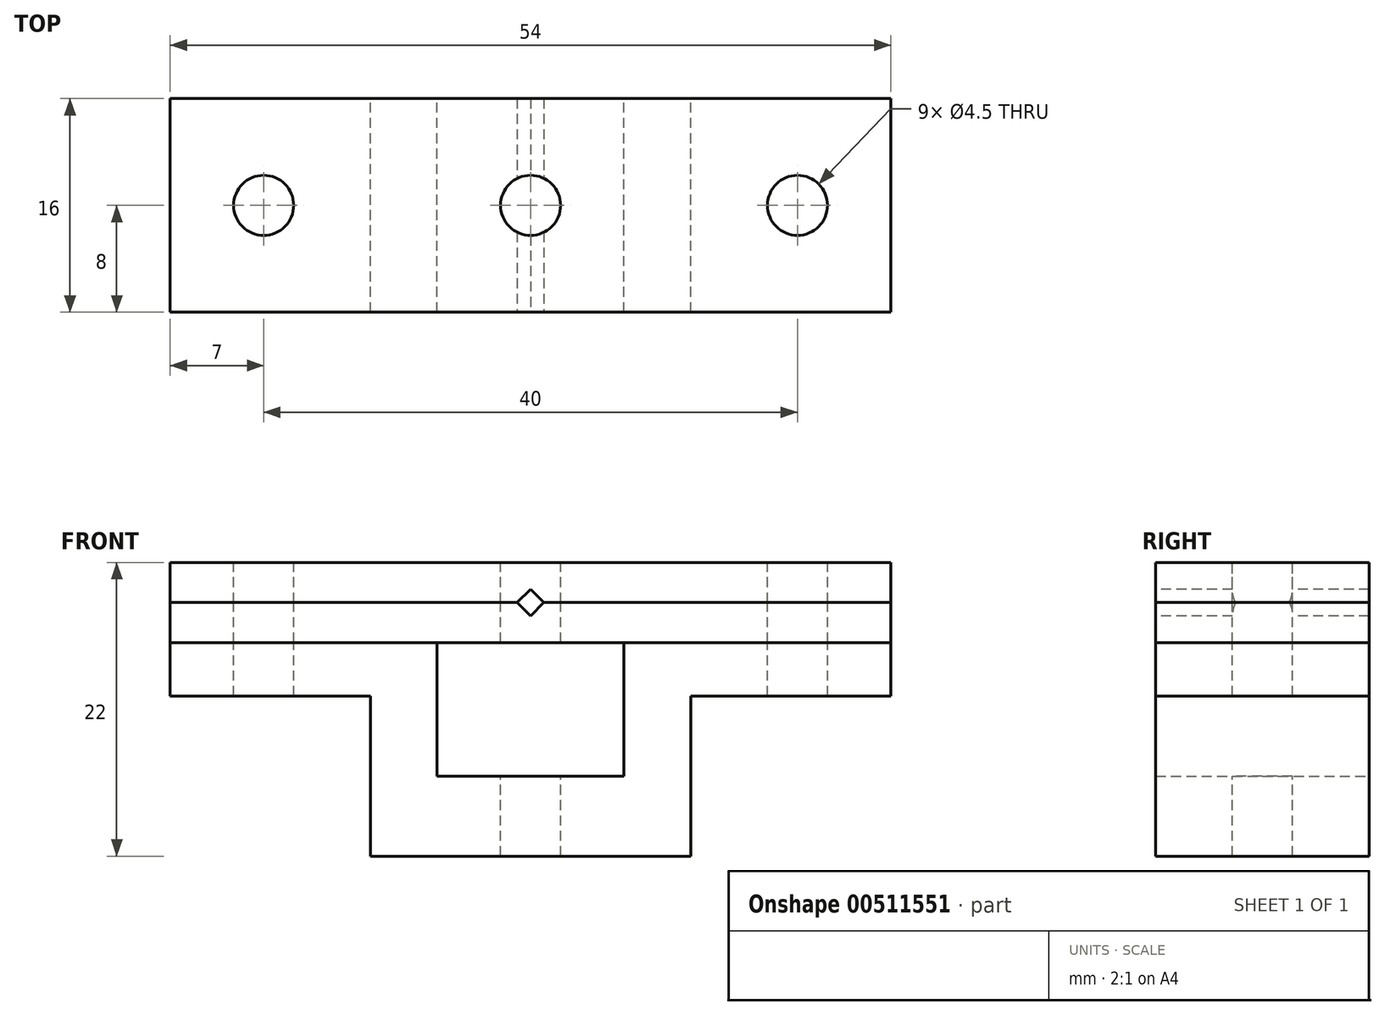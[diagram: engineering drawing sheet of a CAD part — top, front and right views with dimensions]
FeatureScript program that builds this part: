
annotation { "Feature Type Name" : "Feature", "Feature Type Description" : "" }
export const myFeature = defineFeature(function(context is Context, id is Id, definition is map)
    precondition{}
    {
        {
            var Q0;
            Q0=qCreatedBy(makeId("Front.planeOp"),FACE);
            var sketch = newSketch(context, id + "F0", { "sketchPlane" : qUnion([Q0])});
            skLineSegment(sketch, "E0", {"start": v(-7, 0) * mm, "end": v(-7, -10) * mm});
            skLineSegment(sketch, "E1", {"start": v(-7, -10) * mm, "end": v(7, -10) * mm});
            skLineSegment(sketch, "E2", {"start": v(7, -10) * mm, "end": v(7, 0) * mm});
            skLineSegment(sketch, "E3", {"start": v(7, 0) * mm, "end": v(27, 0) * mm});
            skLineSegment(sketch, "E4", {"start": v(27, 0) * mm, "end": v(27, -16) * mm});
            skLineSegment(sketch, "E5", {"start": v(27, -16) * mm, "end": v(-27, -16) * mm});
            skLineSegment(sketch, "E6", {"start": v(-27, -16) * mm, "end": v(-27, 0) * mm});
            skLineSegment(sketch, "E7", {"start": v(-27, 0) * mm, "end": v(-7, 0) * mm});
            skLineSegment(sketch, "E8.bottom", {"start": v(-27, 0) * mm, "end": v(27, 0) * mm});
            skLineSegment(sketch, "E8.top", {"start": v(-27, 3) * mm, "end": v(27, 3) * mm});
            skLineSegment(sketch, "E8.left", {"start": v(-27, 0) * mm, "end": v(-27, 3) * mm});
            skLineSegment(sketch, "E8.right", {"start": v(27, 0) * mm, "end": v(27, 3) * mm});
            skPoint(sketch, "E9.oppositeSnap0", {"position": v(27, 1.5) * mm});
            skLineSegment(sketch, "E9.top", {"start": v(-27, 6) * mm, "end": v(27, 6) * mm});
            skLineSegment(sketch, "E9.left", {"start": v(-27, 3) * mm, "end": v(-27, 6) * mm});
            skLineSegment(sketch, "E9.right", {"start": v(27, 3) * mm, "end": v(27, 6) * mm});
            skSolve(sketch);
        }
        {
            var Q0;
            Q0=makeQuery(id+"F0.imprint","IMPRINT",FACE,{"disambiguationData":[TD([[makeQuery(id+"F0.imprint","IMPRINT",EDGE,{"derivedFrom":sQuery(id+"F0.wireOp",EDGE,"E0")}),-1.0]])]});
            extrude(context, id + "F1", {"entities" : qUnion([Q0]), "endBound" : BoundingType.SYMMETRIC, "depth" : 16 * mm, "offsetDistance" : 25 * mm});
        }
        {
            var Q0;
            Q0=makeQuery(id+"F0.imprint","IMPRINT",FACE,{"disambiguationData":[TD([[makeQuery(id+"F0.imprint","IMPRINT",EDGE,{"derivedFrom":sQuery(id+"F0.wireOp",EDGE,"E3")}),1.0]])]});
            extrude(context, id + "F2", {"entities" : qUnion([Q0]), "endBound" : BoundingType.SYMMETRIC, "depth" : 16 * mm, "offsetDistance" : 25 * mm});
        }
        {
            var Q0;
            Q0=makeQuery(id+"F0.imprint","IMPRINT",FACE,{"disambiguationData":[TD([[makeQuery(id+"F0.imprint","IMPRINT",EDGE,{"derivedFrom":sQuery(id+"F0.wireOp",EDGE,"E8.top")}),1.0]])]});
            extrude(context, id + "F3", {"entities" : qUnion([Q0]), "endBound" : BoundingType.SYMMETRIC, "depth" : 16 * mm, "offsetDistance" : 25 * mm});
        }
        {
            var Q0;
            Q0=makeQuery(id+"F3.opExtrude","SWEPT_FACE",FACE,{"disambiguationData":[OSD([sQuery(id+"F0.wireOp",EDGE,"E9.top")])]});
            var sketch = newSketch(context, id + "F4", { "sketchPlane" : qUnion([Q0])});
            skCircle(sketch, "E10", {"center": v(0, 0) * mm, "radius": 2.25 * mm});
            skCircle(sketch, "E11", {"center": v(-20, 0) * mm, "radius": 2.25 * mm});
            skCircle(sketch, "E12", {"center": v(20, 0) * mm, "radius": 2.25 * mm});
            skSolve(sketch);
        }
        {
            var Q0;
            Q0=makeQuery(id+"F4.imprint","IMPRINT",FACE,{"disambiguationData":[TD([[makeQuery(id+"F4.imprint","IMPRINT",EDGE,{"derivedFrom":sQuery(id+"F4.wireOp",EDGE,"E11")}),1.0]])]});
            var Q1;
            Q1=makeQuery(id+"F4.imprint","IMPRINT",FACE,{"disambiguationData":[TD([[makeQuery(id+"F4.imprint","IMPRINT",EDGE,{"derivedFrom":sQuery(id+"F4.wireOp",EDGE,"E12")}),1.0]])]});
            var Q2;
            Q2=makeQuery(id+"F4.imprint","IMPRINT",FACE,{"disambiguationData":[TD([[makeQuery(id+"F4.imprint","IMPRINT",EDGE,{"derivedFrom":sQuery(id+"F4.wireOp",EDGE,"E10")}),1.0]])]});
            var Q3;
            Q3=sQuery(id+"F4.wireOp",EDGE,"E11");
            extrude(context, id + "F5", {"entities" : qUnion([Q0, Q1, Q2]), "operationType" : NewBodyOperationType.REMOVE, "surfaceEntities" : qUnion([Q3]), "oppositeDirection" : true, "depth" : 30 * mm, "offsetDistance" : 25 * mm});
        }
        {
            var Q0;
            Q0=makeQuery(id+"F3.opExtrude","CAP_FACE",FACE,{"disambiguationData":[OSD([sQuery(id+"F0.wireOp",EDGE,"E8.top"),sQuery(id+"F0.wireOp",EDGE,"E9.top"),sQuery(id+"F0.wireOp",EDGE,"E9.left"),sQuery(id+"F0.wireOp",EDGE,"E9.right")])],"isStart":false});
            var sketch = newSketch(context, id + "F6", { "sketchPlane" : qUnion([Q0])});
            skLineSegment(sketch, "E13", {"start": v(0, 0) * mm, "end": v(0, 10.3) * mm, "construction": true});
            skPoint(sketch, "E13.endSnap0", {"position": v(0, 6) * mm});
            skLineSegment(sketch, "E14", {"start": v(-1, 3) * mm, "end": v(0, 2) * mm});
            skLineSegment(sketch, "E15", {"start": v(0, 2) * mm, "end": v(1, 3) * mm});
            skLineSegment(sketch, "E16", {"start": v(1, 3) * mm, "end": v(0, 4) * mm});
            skLineSegment(sketch, "E17", {"start": v(0, 4) * mm, "end": v(-1, 3) * mm});
            skSolve(sketch);
        }
        {
            var Q0;
            {var subQ0=sQuery(id+"F6.wireOp",EDGE,"E16");Q0=makeQuery(id+"F6.imprint","IMPRINT",FACE,{"disambiguationData":[TD([[makeQuery(id+"F6.imprint","IMPRINT",EDGE,{"derivedFrom":subQ0}),1.0]])]});}
            var Q1;
            {var subQ0=sQuery(id+"F6.wireOp",EDGE,"E14");Q1=makeQuery(id+"F6.imprint","IMPRINT",FACE,{"disambiguationData":[TD([[makeQuery(id+"F6.imprint","IMPRINT",EDGE,{"derivedFrom":subQ0}),1.0]])]});}
            var Q2;
            Q2=sQuery(id+"F6.wireOp",EDGE,"E17");
            var Q3;
            Q3=sQuery(id+"F6.wireOp",EDGE,"E16");
            var Q4;
            Q4=sQuery(id+"F6.wireOp",EDGE,"E15");
            var Q5;
            Q5=sQuery(id+"F6.wireOp",EDGE,"E14");
            extrude(context, id + "F7", {"entities" : qUnion([Q0, Q1]), "operationType" : NewBodyOperationType.REMOVE, "surfaceEntities" : qUnion([Q2, Q3, Q4, Q5]), "oppositeDirection" : true, "depth" : 16 * mm, "offsetDistance" : 25 * mm});
        }
        {
            var Q0;
            Q0=makeQuery(id+"F1.opExtrude","CAP_FACE",FACE,{"disambiguationData":[OSD([sQuery(id+"F0.wireOp",EDGE,"E0"),sQuery(id+"F0.wireOp",EDGE,"E1"),sQuery(id+"F0.wireOp",EDGE,"E2"),sQuery(id+"F0.wireOp",EDGE,"E3"),sQuery(id+"F0.wireOp",EDGE,"E4"),sQuery(id+"F0.wireOp",EDGE,"E5"),sQuery(id+"F0.wireOp",EDGE,"E6"),sQuery(id+"F0.wireOp",EDGE,"E7")])],"isStart":true});
            var sketch = newSketch(context, id + "F8", { "sketchPlane" : qUnion([Q0])});
            skLineSegment(sketch, "E18", {"start": v(-27, 0) * mm, "end": v(-27, -4) * mm});
            skLineSegment(sketch, "E19", {"start": v(-27, -4) * mm, "end": v(-12, -4) * mm});
            skLineSegment(sketch, "E20", {"start": v(-12, -4) * mm, "end": v(-12, -16) * mm});
            skLineSegment(sketch, "E21", {"start": v(-27, -4) * mm, "end": v(-27, -16) * mm});
            skLineSegment(sketch, "E22", {"start": v(-27, -16) * mm, "end": v(-12, -16) * mm});
            skLineSegment(sketch, "E23", {"start": v(12, -16) * mm, "end": v(12, -4) * mm});
            skLineSegment(sketch, "E24", {"start": v(12, -4) * mm, "end": v(27, -4) * mm});
            skLineSegment(sketch, "E25", {"start": v(27, -4) * mm, "end": v(27, -16) * mm});
            skLineSegment(sketch, "E26", {"start": v(27, -16) * mm, "end": v(12, -16) * mm});
            skSolve(sketch);
        }
        {
            var Q0;
            Q0=makeQuery(id+"F8.imprint","IMPRINT",FACE,{"disambiguationData":[TD([[makeQuery(id+"F8.imprint","IMPRINT",EDGE,{"derivedFrom":sQuery(id+"F8.wireOp",EDGE,"E23")}),-1.0]])]});
            var Q1;
            Q1=makeQuery(id+"F8.imprint","IMPRINT",FACE,{"disambiguationData":[TD([[makeQuery(id+"F8.imprint","IMPRINT",EDGE,{"derivedFrom":sQuery(id+"F8.wireOp",EDGE,"E19")}),-1.0]])]});
            extrude(context, id + "F9", {"entities" : qUnion([Q0, Q1]), "operationType" : NewBodyOperationType.REMOVE, "oppositeDirection" : true, "depth" : 25 * mm, "offsetDistance" : 25 * mm});
        }
    });
